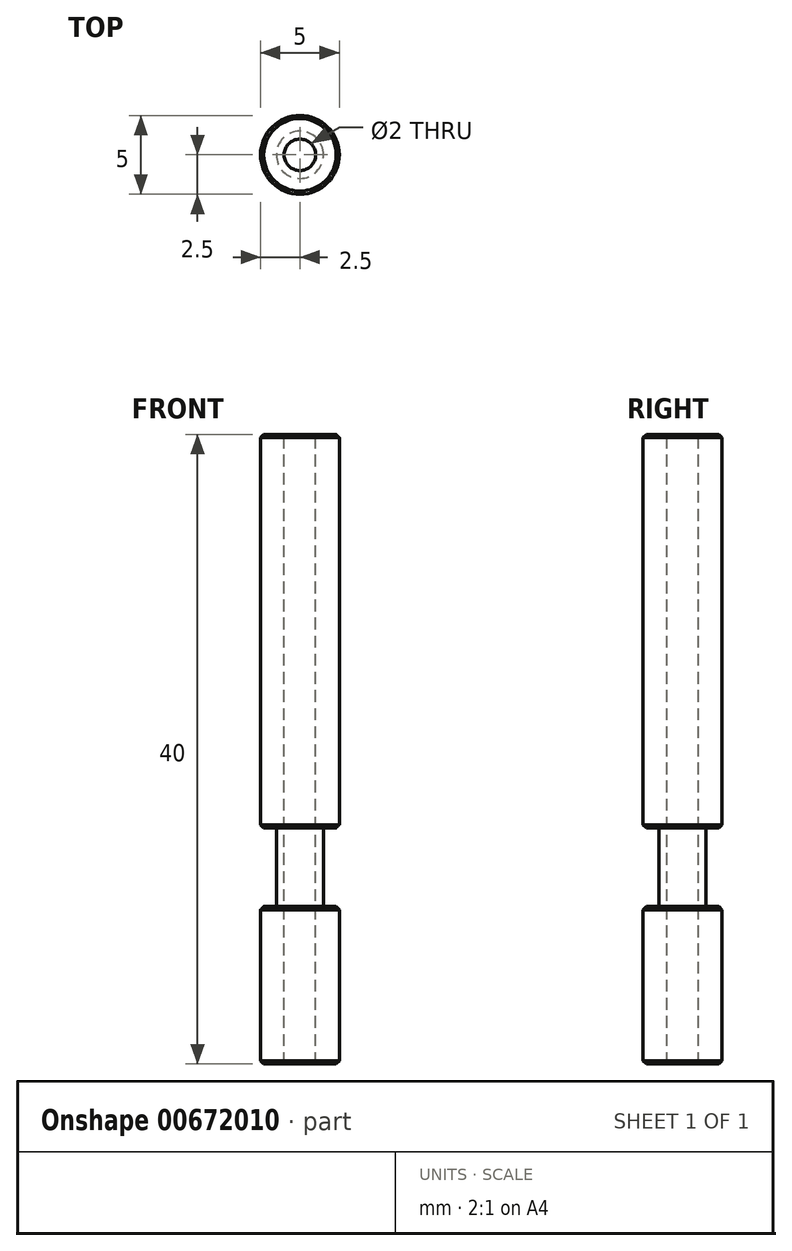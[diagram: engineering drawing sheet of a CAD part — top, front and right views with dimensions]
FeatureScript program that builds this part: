
annotation { "Feature Type Name" : "Feature", "Feature Type Description" : "" }
export const myFeature = defineFeature(function(context is Context, id is Id, definition is map)
    precondition{}
    {
        {
            var Q0;
            Q0=qCreatedBy(makeId("Top.planeOp"),FACE);
            var sketch = newSketch(context, id + "F0", { "sketchPlane" : qUnion([Q0])});
            skCircle(sketch, "E0", {"center": v(0, 0) * mm, "radius": 2.5 * mm});
            skSolve(sketch);
        }
        {
            var Q0;
            Q0=makeQuery(id+"F0.imprint","IMPRINT",FACE,{"disambiguationData":[TD([[makeQuery(id+"F0.imprint","IMPRINT",EDGE,{"derivedFrom":sQuery(id+"F0.wireOp",EDGE,"E0")}),1.0]])]});
            extrude(context, id + "F1", {"entities" : qUnion([Q0]), "depth" : 25 * mm, "offsetDistance" : 25 * mm});
        }
        {
            var Q0;
            Q0=makeQuery(id+"F1.opExtrude","CAP_FACE",FACE,{"disambiguationData":[OSD([sQuery(id+"F0.wireOp",EDGE,"E0")])],"isStart":true});
            var sketch = newSketch(context, id + "F2", { "sketchPlane" : qUnion([Q0])});
            skCircle(sketch, "E1", {"center": v(0, 0) * mm, "radius": 1.5 * mm});
            skSolve(sketch);
        }
        {
            var Q0;
            Q0=makeQuery(id+"F2.imprint","IMPRINT",FACE,{"disambiguationData":[TD([[makeQuery(id+"F2.imprint","IMPRINT",EDGE,{"derivedFrom":sQuery(id+"F2.wireOp",EDGE,"E1")}),1.0]])]});
            extrude(context, id + "F3", {"entities" : qUnion([Q0]), "operationType" : NewBodyOperationType.ADD, "depth" : 5 * mm, "offsetDistance" : 25 * mm});
        }
        {
            var Q0;
            Q0=makeQuery(id+"F3.opExtrude","CAP_FACE",FACE,{"disambiguationData":[OSD([sQuery(id+"F2.wireOp",EDGE,"E1")])],"isStart":false});
            var sketch = newSketch(context, id + "F4", { "sketchPlane" : qUnion([Q0])});
            skCircle(sketch, "E2", {"center": v(0, 0) * mm, "radius": 2.5 * mm});
            skSolve(sketch);
        }
        {
            var Q0;
            Q0=makeQuery(id+"F4.imprint","IMPRINT",FACE,{"disambiguationData":[TD([[makeQuery(id+"F4.imprint","IMPRINT",EDGE,{"derivedFrom":sQuery(id+"F4.wireOp",EDGE,"E2")}),1.0]])]});
            var Q1;
            Q1=makeQuery(id+"F4.imprint","IMPRINT",FACE,{"disambiguationData":[TD([[makeQuery(id+"F4.imprint","IMPRINT",EDGE,{"derivedFrom":makeQuery(id+"F3.opExtrude","CAP_EDGE",EDGE,{"disambiguationData":[OSD([sQuery(id+"F2.wireOp",EDGE,"E1")])],"isStart":false})}),1.0]])]});
            extrude(context, id + "F5", {"entities" : qUnion([Q0, Q1]), "operationType" : NewBodyOperationType.ADD, "depth" : 10 * mm, "offsetDistance" : 25 * mm});
        }
        {
            var Q0;
            Q0=makeQuery(id+"F1.opExtrude","CAP_FACE",FACE,{"disambiguationData":[OSD([sQuery(id+"F0.wireOp",EDGE,"E0")])],"isStart":false});
            var sketch = newSketch(context, id + "F6", { "sketchPlane" : qUnion([Q0])});
            skPoint(sketch, "E3", {"position": v(0, 0) * mm});
            skSolve(sketch);
        }
        {
            var Q0;
            Q0=sQuery(id+"F6.wireOp",VERTEX,"E3");
            var Q1;
            Q1=makeQuery(id+"F1.opExtrude","SWEPT_BODY",BODY,{"disambiguationData":[OSD([sQuery(id+"F0.wireOp",EDGE,"E0")])]});
            hole(context, id + "F7", {"style" : HoleStyle.SIMPLE, "endStyle" : HoleEndStyle.THROUGH, "holeDiameter" : 2 * mm, "majorDiameter" : 5 * mm, "isTappedThrough" : true, "tappedDepth" : 7.6 * mm, "tapClearance" : 3, "startFromSketch" : true, "locations" : qUnion([Q0]), "scope" : qUnion([Q1])});
        }
        {
            var Q0;
            Q0=makeQuery(id+"F1.opExtrude","CAP_EDGE",EDGE,{"disambiguationData":[OSD([sQuery(id+"F0.wireOp",EDGE,"E0")])],"isStart":false});
            var Q1;
            Q1=makeQuery(id+"F5.opExtrude","CAP_EDGE",EDGE,{"disambiguationData":[OSD([sQuery(id+"F4.wireOp",EDGE,"E2")])],"isStart":true});
            var Q2;
            Q2=makeQuery(id+"F5.opExtrude","CAP_EDGE",EDGE,{"disambiguationData":[OSD([sQuery(id+"F4.wireOp",EDGE,"E2")])],"isStart":false});
            var Q3;
            Q3=makeQuery(id+"F1.opExtrude","CAP_EDGE",EDGE,{"disambiguationData":[OSD([sQuery(id+"F0.wireOp",EDGE,"E0")])],"isStart":true});
            chamfer(context, id + "F8", {"entities" : qUnion([Q0, Q1, Q2, Q3]), "width" : .2 * mm, "tangentPropagation" : true});
        }
    });
